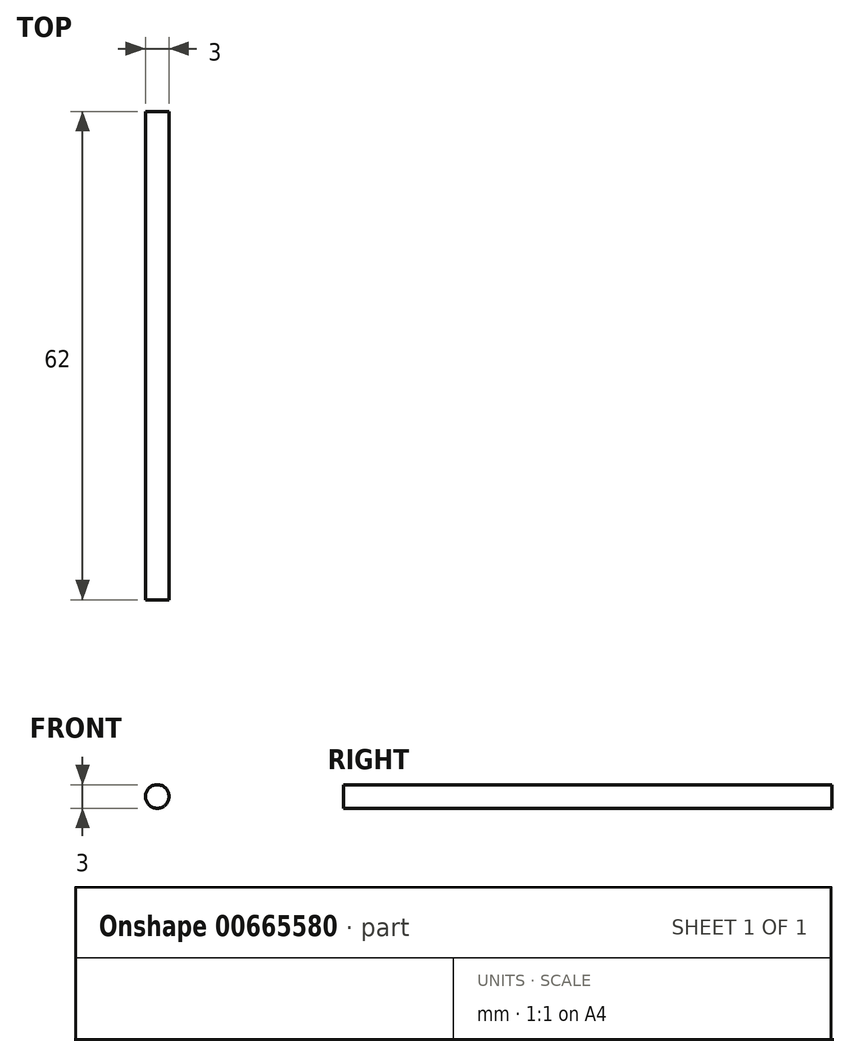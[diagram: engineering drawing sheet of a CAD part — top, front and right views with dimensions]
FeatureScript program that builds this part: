
annotation { "Feature Type Name" : "Feature", "Feature Type Description" : "" }
export const myFeature = defineFeature(function(context is Context, id is Id, definition is map)
    precondition{}
    {
        {
            var Q0;
            Q0=qCreatedBy(makeId("Front.planeOp"),FACE);
            var sketch = newSketch(context, id + "F0", { "sketchPlane" : qUnion([Q0])});
            skCircle(sketch, "E0", {"center": v(0, 0) * mm, "radius": 1.5 * mm});
            skSolve(sketch);
        }
        {
            var Q0;
            Q0=qSketchRegion(id+"F0",true);
            extrude(context, id + "F1", {"entities" : qUnion([Q0]), "endBound" : BoundingType.SYMMETRIC, "depth" : 62 * mm, "offsetDistance" : 25 * mm});
        }
    });
